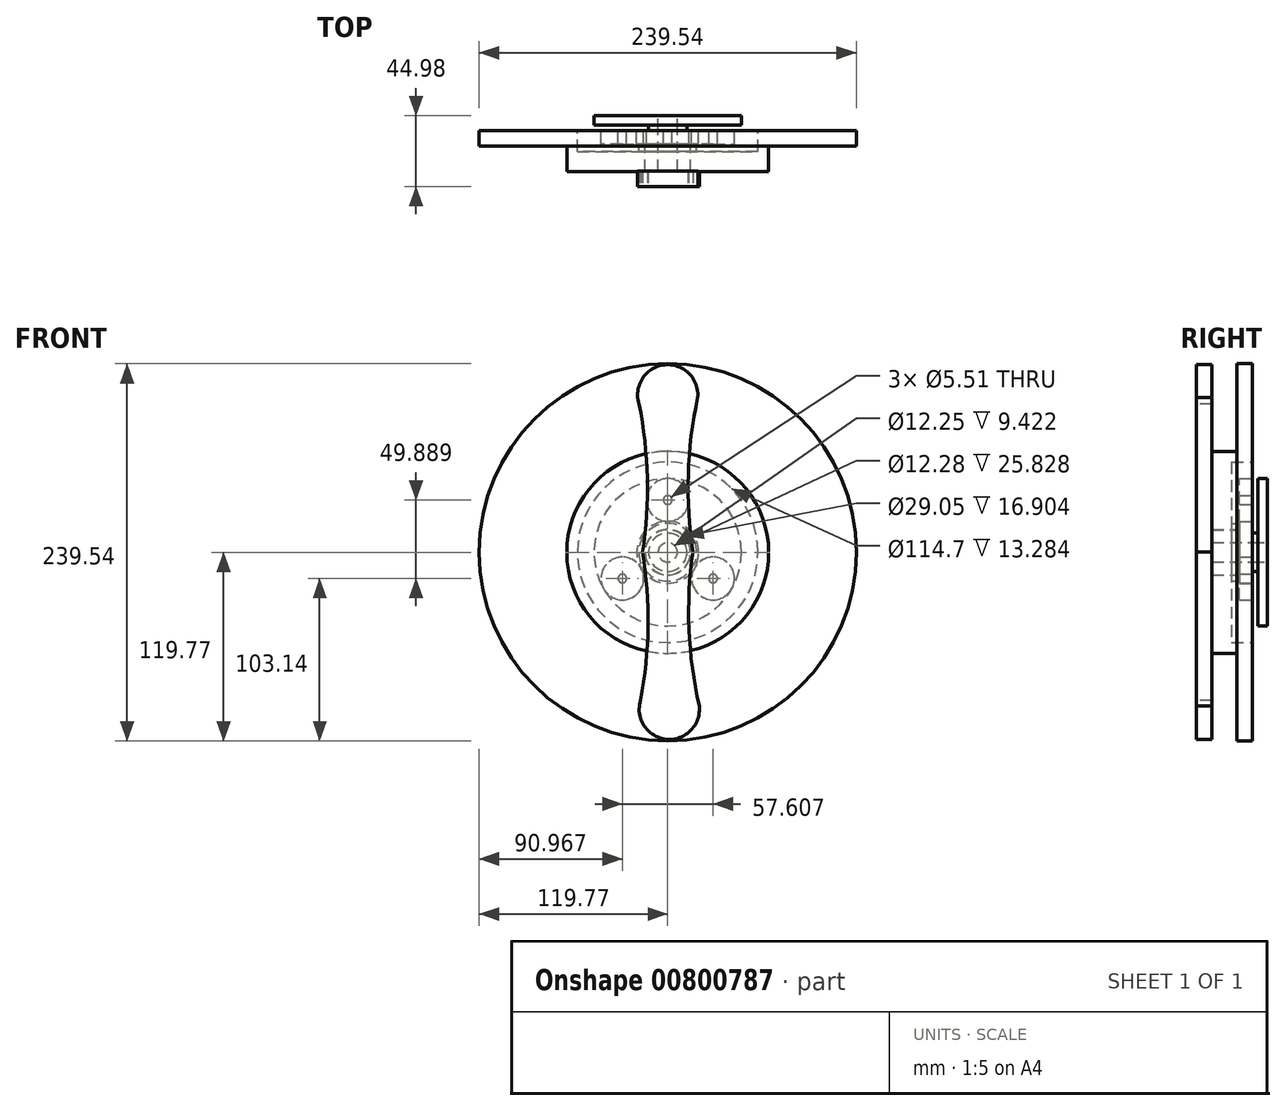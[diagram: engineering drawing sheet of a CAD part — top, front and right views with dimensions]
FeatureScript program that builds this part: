
annotation { "Feature Type Name" : "Feature", "Feature Type Description" : "" }
export const myFeature = defineFeature(function(context is Context, id is Id, definition is map)
    precondition{}
    {
        {
            var Q0;
            Q0=qCreatedBy(makeId("Right.planeOp"),FACE);
            var sketch = newSketch(context, id + "F0", { "sketchPlane" : qUnion([Q0])});
            skLineSegment(sketch, "E0", {"start": v(0, 8.26) * mm, "end": v(0, 19.69) * mm});
            skLineSegment(sketch, "E1", {"start": v(0, 19.69) * mm, "end": v(-8.48, 19.69) * mm});
            skLineSegment(sketch, "E2", {"start": v(-8.48, 19.69) * mm, "end": v(-8.48, 14.33) * mm});
            skLineSegment(sketch, "E3", {"start": v(-8.48, 14.33) * mm, "end": v(-25.83, 14.33) * mm});
            skLineSegment(sketch, "E4", {"start": v(-25.83, 14.33) * mm, "end": v(-25.83, 100.06) * mm});
            skLineSegment(sketch, "E5", {"start": v(-25.83, 100.06) * mm, "end": v(-35.56, 100.06) * mm});
            skLineSegment(sketch, "E6", {"start": v(-35.56, 100.06) * mm, "end": v(-35.56, 6.14) * mm});
            skLineSegment(sketch, "E7", {"start": v(-35.56, 6.14) * mm, "end": v(0, 6.14) * mm});
            skLineSegment(sketch, "E8", {"start": v(0, 6.14) * mm, "end": v(0, 8.26) * mm});
            skPoint(sketch, "E9.endSnap0", {"position": v(-17.15, 14.33) * mm});
            skLineSegment(sketch, "E10", {"start": v(0, 0) * mm, "end": v(-48.81, 0) * mm});
            skSolve(sketch);
        }
        {
            var Q0;
            Q0=makeQuery(id+"F0.imprint","IMPRINT",FACE,{"disambiguationData":[TD([[makeQuery(id+"F0.imprint","IMPRINT",EDGE,{"derivedFrom":sQuery(id+"F0.wireOp",EDGE,"E0")}),1.0]])]});
            var Q1;
            Q1=sQuery(id+"F0.wireOp",EDGE,"E10");
            revolve(context, id + "F1", {"surfaceOperationType" : NewSurfaceOperationType.NEW, "entities" : qUnion([Q0]), "axis" : qUnion([Q1]), "revolveType" : RevolveType.FULL});
        }
        {
            var Q0;
            Q0=makeQuery(id+"F1.opRevolve","SWEPT_FACE",FACE,{"disambiguationData":[OSD([sQuery(id+"F0.wireOp",EDGE,"E6")])]});
            var sketch = newSketch(context, id + "F2", { "sketchPlane" : qUnion([Q0])});
            skCircle(sketch, "E11", {"center": v(0, 0) * mm, "radius": 100.06 * mm, "construction": true});
            skArc(sketch, "E12", {"start": v(19.04, 98.23) * mm, "mid": v(-2.08, 119.08) * mm, "end": v(-18.2, 94.16) * mm});
            skArc(sketch, "E13", {"start": v(-15.94, 0) * mm, "mid": v(-13.05, 49.26) * mm, "end": v(-19.04, 98.23) * mm});
            skLineSegment(sketch, "E14", {"start": v(0, 0) * mm, "end": v(0, 47.96) * mm});
            skArc(sketch, "E15.MirrorCS", {"start": v(15.94, 0) * mm, "mid": v(13.05, 49.26) * mm, "end": v(19.04, 98.23) * mm});
            skLineSegment(sketch, "E16", {"start": v(0.9, 0.18) * mm, "end": v(-34.21, 0) * mm});
            skArc(sketch, "E17.MirrorCS", {"start": v(-15.94, 0.18) * mm, "mid": v(-12.56, -49.04) * mm, "end": v(-18.06, -98.07) * mm});
            skArc(sketch, "E18.MirrorCS", {"start": v(15.94, 0.5) * mm, "mid": v(13.54, -48.78) * mm, "end": v(20.02, -97.7) * mm});
            skArc(sketch, "E19.MirrorCS", {"start": v(20.02, -97.7) * mm, "mid": v(-0.89, -118.75) * mm, "end": v(-17.26, -94) * mm});
            skSolve(sketch);
        }
        {
            var Q0;
            {var subQ3=sQuery(id+"F2.wireOp",EDGE,"E13");var subQ5=sQuery(id+"F2.wireOp",EDGE,"E12");var subQ6=makeQuery(id+"F2.imprint","INTERSECT",VERTEX,{"derivedFrom":[subQ5,subQ3]});Q0=makeQuery(id+"F2.imprint","IMPRINT",FACE,{"disambiguationData":[TD([[makeQuery(id+"F2.imprint","IMPRINT",EDGE,{"disambiguationData":[TD([[subQ6,1.0]])],"derivedFrom":subQ3}),1.0]])]});}
            var Q1;
            {var subQ3=sQuery(id+"F2.wireOp",EDGE,"E19.MirrorCS");var subQ5=sQuery(id+"F2.wireOp",EDGE,"E18.MirrorCS");var subQ7=makeQuery(id+"F2.imprint","INTERSECT",VERTEX,{"derivedFrom":[subQ5,subQ3]});Q1=makeQuery(id+"F2.imprint","IMPRINT",FACE,{"disambiguationData":[TD([[makeQuery(id+"F2.imprint","IMPRINT",EDGE,{"disambiguationData":[TD([[subQ7,1.0]])],"derivedFrom":subQ5}),1.0]])]});}
            extrude(context, id + "F3", {"entities" : qUnion([Q0, Q1]), "operationType" : NewBodyOperationType.REMOVE, "oppositeDirection" : true, "depth" : 25 * mm, "offsetDistance" : 25 * mm});
        }
        {
            var Q0;
            Q0 = qSketchRegion(id + "F2", true);
            var Q1;
            Q1=makeQuery(id+"F1.opRevolve","SWEPT_FACE",FACE,{"disambiguationData":[OSD([sQuery(id+"F0.wireOp",EDGE,"E4")])]});
            extrude(context, id + "F4", {"entities" : qUnion([Q0]), "operationType" : NewBodyOperationType.ADD, "endBound" : BoundingType.UP_TO_SURFACE, "oppositeDirection" : true, "depth" : 25 * mm, "endBoundEntityFace" : qUnion([Q1]), "offsetDistance" : 25 * mm});
        }
        {
            var Q0;
            Q0=makeQuery(id+"F1.opRevolve","SWEPT_FACE",FACE,{"disambiguationData":[OSD([sQuery(id+"F0.wireOp",EDGE,"E0"),sQuery(id+"F0.wireOp",EDGE,"E8")])]});
            var sketch = newSketch(context, id + "F5", { "sketchPlane" : qUnion([Q0])});
            skCircle(sketch, "E20", {"center": v(0, 0) * mm, "radius": 33.26 * mm, "construction": true});
            skCircle(sketch, "E21", {"center": v(0, 33.26) * mm, "radius": 13.57 * mm});
            skCircle(sketch, "E22.1.0", {"center": v(-28.8, -16.63) * mm, "radius": 13.57 * mm});
            skCircle(sketch, "E22.2.0", {"center": v(28.8, -16.63) * mm, "radius": 13.57 * mm});
            skCircle(sketch, "E23", {"center": v(0, 33.26) * mm, "radius": 2.75 * mm});
            skCircle(sketch, "E24.1.0", {"center": v(-28.8, -16.63) * mm, "radius": 2.75 * mm});
            skCircle(sketch, "E24.2.0", {"center": v(28.8, -16.63) * mm, "radius": 2.75 * mm});
            skSolve(sketch);
        }
        {
            var Q0;
            Q0=makeQuery(id+"F5.imprint","IMPRINT",FACE,{"disambiguationData":[TD([[makeQuery(id+"F5.imprint","IMPRINT",EDGE,{"derivedFrom":sQuery(id+"F5.wireOp",EDGE,"E21")}),1.0]])]});
            var Q1;
            Q1=makeQuery(id+"F5.imprint","IMPRINT",FACE,{"disambiguationData":[TD([[makeQuery(id+"F5.imprint","IMPRINT",EDGE,{"derivedFrom":sQuery(id+"F5.wireOp",EDGE,"E22.1.0")}),1.0]])]});
            var Q2;
            Q2=makeQuery(id+"F5.imprint","IMPRINT",FACE,{"disambiguationData":[TD([[makeQuery(id+"F5.imprint","IMPRINT",EDGE,{"derivedFrom":sQuery(id+"F5.wireOp",EDGE,"E22.2.0")}),1.0]])]});
            var Q3;
            Q3=makeQuery(id+"F1.opRevolve","SWEPT_FACE",FACE,{"disambiguationData":[OSD([sQuery(id+"F0.wireOp",EDGE,"E2")])]});
            extrude(context, id + "F6", {"entities" : qUnion([Q0, Q1, Q2]), "operationType" : NewBodyOperationType.ADD, "endBound" : BoundingType.UP_TO_SURFACE, "oppositeDirection" : true, "depth" : 25 * mm, "endBoundEntityFace" : qUnion([Q3]), "offsetDistance" : 25 * mm});
        }
        {
            var Q0;
            Q0=qCreatedBy(makeId("Right.planeOp"),FACE);
            var sketch = newSketch(context, id + "F7", { "sketchPlane" : qUnion([Q0])});
            skLineSegment(sketch, "E25", {"start": v(0, 6.12) * mm, "end": v(9.42, 6.12) * mm});
            skLineSegment(sketch, "E26", {"start": v(9.42, 6.12) * mm, "end": v(9.42, 46.85) * mm});
            skLineSegment(sketch, "E27", {"start": v(9.42, 46.85) * mm, "end": v(3.5, 46.85) * mm});
            skLineSegment(sketch, "E28", {"start": v(3.5, 46.85) * mm, "end": v(3.5, 12.15) * mm});
            skLineSegment(sketch, "E29", {"start": v(3.5, 12.15) * mm, "end": v(0, 12.15) * mm});
            skLineSegment(sketch, "E30", {"start": v(0, 12.15) * mm, "end": v(0, 6.12) * mm});
            skLineSegment(sketch, "E31", {"start": v(-25.92, 21.75) * mm, "end": v(-25.92, 14.52) * mm});
            skLineSegment(sketch, "E32", {"start": v(-25.92, 14.52) * mm, "end": v(-8.92, 14.52) * mm});
            skLineSegment(sketch, "E33", {"start": v(-8.92, 14.52) * mm, "end": v(-8.92, 18.33) * mm});
            skLineSegment(sketch, "E34", {"start": v(-8.92, 18.33) * mm, "end": v(-13.28, 18.33) * mm});
            skLineSegment(sketch, "E35", {"start": v(-13.28, 18.33) * mm, "end": v(-13.28, 57.35) * mm});
            skLineSegment(sketch, "E36", {"start": v(-13.28, 57.35) * mm, "end": v(0, 57.35) * mm});
            skLineSegment(sketch, "E37", {"start": v(0, 57.35) * mm, "end": v(0, 119.77) * mm});
            skLineSegment(sketch, "E38", {"start": v(0, 119.77) * mm, "end": v(-9.9, 119.77) * mm});
            skLineSegment(sketch, "E39", {"start": v(-9.9, 119.77) * mm, "end": v(-9.9, 64.12) * mm});
            skLineSegment(sketch, "E40", {"start": v(-9.9, 64.12) * mm, "end": v(-25.92, 64.12) * mm});
            skLineSegment(sketch, "E41", {"start": v(-25.92, 64.12) * mm, "end": v(-25.92, 21.75) * mm});
            skLineSegment(sketch, "E42", {"start": v(0, 0) * mm, "end": v(-49.1, 0) * mm});
            skSolve(sketch);
        }
        {
            var Q0;
            Q0 = qSketchRegion(id + "F7", true);
            var Q1;
            Q1=sQuery(id+"F7.wireOp",EDGE,"E42");
            revolve(context, id + "F8", {"operationType" : NewBodyOperationType.ADD, "surfaceOperationType" : NewSurfaceOperationType.NEW, "entities" : qUnion([Q0]), "axis" : qUnion([Q1]), "revolveType" : RevolveType.FULL});
        }
    });
